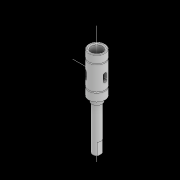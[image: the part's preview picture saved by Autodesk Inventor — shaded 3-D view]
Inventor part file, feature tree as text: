
AUTODESK INVENTOR PART (.ipt)
format: ipt  version: 2021 (Build 250183000, 183)  size: 297,984 bytes
history: native  units: mm
features: sketch x11, extrude x7, other x5, plane x4, revolve x3, chamfer x3, pattern_circular x2, hole x1
ambient origin geometry x8: Origin, YZ Plane, XZ Plane, XY Plane, X Axis, Y Axis, Z Axis, Center Point
bodies: Solid1 (feature_tree)
feature tree (36):
  revolve  "Revolution1"  [1 undecoded]
  plane  "Work Plane1"
  extrude  "Extrusion1"  TaperAngle=90.0deg  [1 undecoded]
  chamfer  "Chamfer1"  Distance=10.0mm
  pattern_circular  "Circular Pattern1"  Count=3 Angle=360.0deg
  plane  "Work Plane2"
  extrude  "Extrusion2"  Depth=0.1mm
  extrude  "Extrusion4"  Depth=10.0mm
  extrude  "Extrusion5"  Depth=2.5mm TaperAngle=0.0deg
  other  "Work Axis1"
  revolve  "Revolution2"  [1 undecoded]
  extrude  "Extrusion6"  TaperAngle=90.0deg  [1 undecoded]
  other  "Work Axis2"
  chamfer  "Chamfer4"  Distance=10.0mm
  revolve  "Revolution3"  Angle=45.0deg
  chamfer  "Chamfer5"  Distance=0.5mm
  other  "Work Axis3"
  plane  "Work Plane3"
  hole  "Hole1"  [1 undecoded]
  extrude  "Extrusion8"  Depth=10.0mm TaperAngle=45.0deg
  plane  "Work Plane4"
  extrude  "Extrusion9"  Depth=10.0mm
  pattern_circular  "Circular Pattern2"  [2 undecoded]
  sketch  "Sketch1"  dims[d0=8.0mm d2=20.0mm d5=5.5mm]
  sketch  "Sketch2"  dims[d6=16.0mm d7=90.0deg]
  sketch  "Sketch3"  dims[d8=10.5mm]
  other  "Srf1"
  sketch  "Sketch5"  dims[d9=2.0mm]
  sketch  "Sketch6"  dims[d10=2.5mm d11=10.0mm d12=0.0mm]
  sketch  "Sketch7"  dims[d13=0.5mm d14=2.0mm d15=45.0deg d16=30.0mm d17=360.0deg]
  sketch  "Sketch8"  dims[d19=90.0deg d20=0.1mm]
  sketch  "Sketch10"  dims[d21=10.0mm d22=0.0mm d24=1.0mm]
  sketch  "Sketch11"  dims[d28=5.0mm d29=2.5mm d30=0.0mm]
  sketch  "Sketch12"  dims[d33=4.0mm d34=22.0mm d35=0.0mm]
  sketch  "Sketch13"  dims[d42=0.25mm d43=90.0deg d44=10.0mm d45=0.0mm d53=0.25mm d54=2.0mm d55=45.0deg d57=0.5mm d59=90.0deg d60=0.25mm d61=2.0mm d62=45.0deg d63=8.0mm d66=0.5mm d70=4.4mm d71=3.0mm d72=5.5mm d73=6.0mm d74=4.0mm d75=2.0mm d76=90.0deg d77=18.0mm d78=20.594885mm d81=4.0mm d82=16.0mm d83=0.5mm d84=6.0mm d85=10.0mm d86=0.0mm d90=2.66mm d91=1.6mm d92=10.0mm d93=0.0mm d94=30.0mm d95=360.0deg]
  other  "Unwrap1"
note: 7 required parameter values undecoded (feature->parameter linkage not recoverable at this tier; creation-order binding heuristic only, values carry confidence <= 0.55)